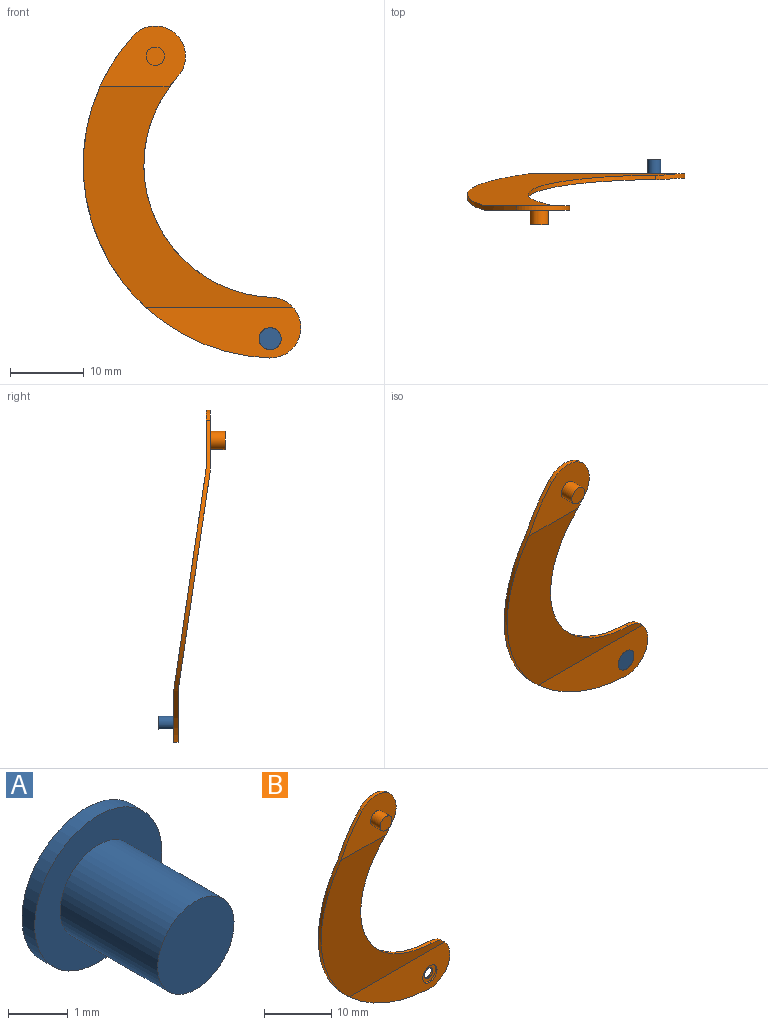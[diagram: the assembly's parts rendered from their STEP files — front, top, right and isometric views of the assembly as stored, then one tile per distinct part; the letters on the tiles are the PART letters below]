
ASSEMBLY  parts=2 mates=1
PART A: 5 faces, bbox 3x2.6x3 mm
  f0: cylinder r=1.5mm len=3mm, axis (0,1,0), area 2.8mm2, adj f1,f2
  f1: plane 3x3mm, normal (0,-1,0), area 4.5mm2, adj f0,f3
  f2: plane 3x3mm, normal (0,1,0), area 7.1mm2, adj f0
  f3: cylinder r=0.9mm len=2.3mm, axis (0,1,0), area 13mm2, adj f1,f4
  f4: plane 1.8x1.8mm, normal (0,-1,0), area 2.5mm2, adj f3
PART B: 15 faces, bbox 29.6x7x45.2 mm
  f0: cylinder r=0.9mm len=1.8mm, axis (0,1,0), area 1.7mm2, adj f6,f14
  f1: cylinder r=4.12mm len=7.19mm, axis (0,1,0), area 7.5mm2, adj f2,f4,f5,f9
  f2: cylinder r=26.25mm len=43.8mm, axis (0,1,0), area 35.5mm2, adj f1,f3,f5,f6,f7,f8,f9,f10
  f3: cylinder r=4.12mm len=8.25mm, axis (0,1,0), area 7.8mm2, adj f2,f4,f6,f7,f8,f10
  f4: cylinder r=18mm len=30.03mm, axis (0,1,0), area 24.5mm2, adj f1,f3,f5,f8,f9,f10
  f5: plane 11.62x8.16mm, normal (0,-1,0), area 62.7mm2, adj f1,f2,f4,f8,f11
  f6: plane 21.12x6.91mm, normal (0,1,0), area 100.6mm2, adj f0,f2,f3,f10
  f7: plane 21.12x6.91mm, normal (0,-1,0), area 96mm2, adj f2,f3,f8,f13
  f8: plane 30.09x28.52mm, normal (0,-0.99,-0.14), area 300.1mm2, adj f2,f3,f4,f5,f7
  f9: plane 11.55x8mm, normal (0,1,0), area 66mm2, adj f1,f2,f4,f10
  f10: plane 30.25x28.52mm, normal (0,0.99,0.14), area 301.7mm2, adj f2,f3,f4,f6,f9
  f11: cylinder r=1.25mm len=2.5mm, axis (0,1,0), area 15.7mm2, adj f5,f12
  f12: plane 2.5x2.5mm, normal (0,-1,0), area 4.9mm2, adj f11
  f13: cylinder r=1.5mm len=3mm, axis (0,-1,0), area 2.8mm2, adj f7,f14
  f14: plane 3x3mm, normal (0,-1,0), area 4.5mm2, adj f0,f13
PLACE A rot(axis=(-1,0,0),180deg) t=(24.38,8.7,-10.08)mm
PLACE B t=(-41.24,9.3,57.21)mm
MATE fastened B.f0 <-> A.f0  axis (0,-1,0) through (14.38,9,0.92)mm
